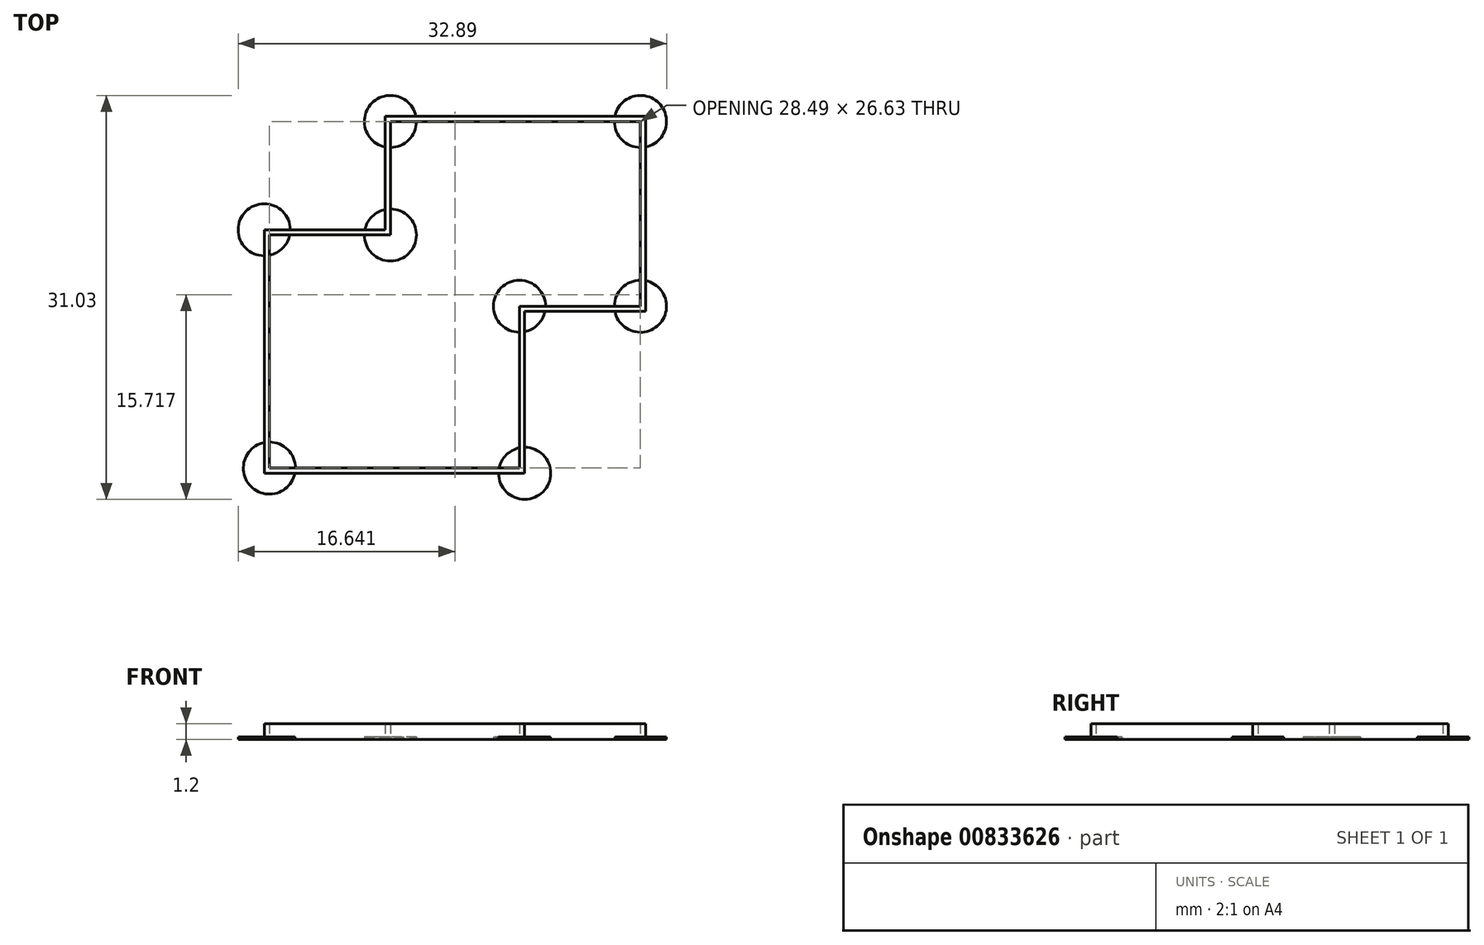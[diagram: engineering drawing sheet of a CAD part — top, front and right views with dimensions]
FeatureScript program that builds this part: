
annotation { "Feature Type Name" : "Feature", "Feature Type Description" : "" }
export const myFeature = defineFeature(function(context is Context, id is Id, definition is map)
    precondition{}
    {
        {
            var Q0;
            Q0=qCreatedBy(makeId("Top.planeOp"),FACE);
            var sketch = newSketch(context, id + "F0", { "sketchPlane" : qUnion([Q0])});
            skLineSegment(sketch, "E0.bottom", {"start": v(-13.81, 9.48) * mm, "end": v(-4.52, 9.48) * mm});
            skLineSegment(sketch, "E0.top", {"start": v(-13.81, -9.23) * mm, "end": v(6.19, -9.23) * mm});
            skLineSegment(sketch, "E0.left", {"start": v(-13.81, 9.48) * mm, "end": v(-13.81, -9.23) * mm});
            skLineSegment(sketch, "E0.right", {"start": v(6.19, 3.2) * mm, "end": v(6.19, -9.23) * mm});
            skLineSegment(sketch, "E1.bottom", {"start": v(-4.52, 18.2) * mm, "end": v(15.48, 18.2) * mm});
            skLineSegment(sketch, "E1.top", {"start": v(6.19, 3.2) * mm, "end": v(15.48, 3.2) * mm});
            skLineSegment(sketch, "E1.left", {"start": v(-4.52, 18.2) * mm, "end": v(-4.52, 9.48) * mm});
            skLineSegment(sketch, "E1.right", {"start": v(15.48, 18.2) * mm, "end": v(15.48, 3.2) * mm});
            skLineSegment(sketch, "E2.0", {"start": v(-4.12, 17.8) * mm, "end": v(-4.12, 9.08) * mm});
            skLineSegment(sketch, "E2.1", {"start": v(-13.41, 9.08) * mm, "end": v(-4.12, 9.08) * mm});
            skLineSegment(sketch, "E2.2", {"start": v(-4.12, 17.8) * mm, "end": v(15.08, 17.8) * mm});
            skLineSegment(sketch, "E2.3", {"start": v(-13.41, 9.08) * mm, "end": v(-13.41, -8.83) * mm});
            skLineSegment(sketch, "E2.4", {"start": v(15.08, 17.8) * mm, "end": v(15.08, 3.6) * mm});
            skLineSegment(sketch, "E2.5", {"start": v(5.79, 3.6) * mm, "end": v(15.08, 3.6) * mm});
            skLineSegment(sketch, "E2.6", {"start": v(5.79, 3.6) * mm, "end": v(5.79, -8.83) * mm});
            skLineSegment(sketch, "E2.7", {"start": v(-13.41, -8.83) * mm, "end": v(5.79, -8.83) * mm});
            skSolve(sketch);
        }
        {
            var Q0;
            Q0=makeQuery(id+"F0.imprint","IMPRINT",FACE,{"disambiguationData":[TD([[makeQuery(id+"F0.imprint","IMPRINT",EDGE,{"derivedFrom":sQuery(id+"F0.wireOp",EDGE,"E0.bottom")}),-1.0]])]});
            extrude(context, id + "F1", {"entities" : qUnion([Q0]), "depth" : 1.2 * mm, "offsetDistance" : 25 * mm});
        }
        {
            var Q0;
            Q0=makeQuery(id+"F1.opExtrude","CAP_FACE",FACE,{"disambiguationData":[OSD([sQuery(id+"F0.wireOp",EDGE,"E0.bottom"),sQuery(id+"F0.wireOp",EDGE,"E0.top"),sQuery(id+"F0.wireOp",EDGE,"E0.left"),sQuery(id+"F0.wireOp",EDGE,"E0.right"),sQuery(id+"F0.wireOp",EDGE,"E1.bottom"),sQuery(id+"F0.wireOp",EDGE,"E1.top"),sQuery(id+"F0.wireOp",EDGE,"E1.left"),sQuery(id+"F0.wireOp",EDGE,"E1.right"),sQuery(id+"F0.wireOp",EDGE,"E2.0"),sQuery(id+"F0.wireOp",EDGE,"E2.1"),sQuery(id+"F0.wireOp",EDGE,"E2.2"),sQuery(id+"F0.wireOp",EDGE,"E2.3"),sQuery(id+"F0.wireOp",EDGE,"E2.4"),sQuery(id+"F0.wireOp",EDGE,"E2.5"),sQuery(id+"F0.wireOp",EDGE,"E2.6"),sQuery(id+"F0.wireOp",EDGE,"E2.7")])],"isStart":true});
            var sketch = newSketch(context, id + "F2", { "sketchPlane" : qUnion([Q0])});
            skCircle(sketch, "E3", {"center": v(-13.41, 8.83) * mm, "radius": 2 * mm});
            skCircle(sketch, "E4", {"center": v(15.08, -3.6) * mm, "radius": 2 * mm});
            skCircle(sketch, "E5", {"center": v(15.08, -17.8) * mm, "radius": 2 * mm});
            skCircle(sketch, "E6", {"center": v(-4.12, -17.8) * mm, "radius": 2 * mm});
            skCircle(sketch, "E7", {"center": v(6.19, 9.23) * mm, "radius": 2 * mm});
            skCircle(sketch, "E8", {"center": v(-13.81, -9.48) * mm, "radius": 2 * mm});
            skCircle(sketch, "E9", {"center": v(-4.12, -9.08) * mm, "radius": 2 * mm});
            skCircle(sketch, "E10", {"center": v(5.79, -3.6) * mm, "radius": 2 * mm});
            skSolve(sketch);
        }
        {
            var Q0;
            {var subQ1=makeQuery(id+"F1.opExtrude","CAP_EDGE",EDGE,{"disambiguationData":[OSD([sQuery(id+"F0.wireOp",EDGE,"E0.top")])],"isStart":true});var subQ3=sQuery(id+"F2.wireOp",EDGE,"E3");var subQ7=makeQuery(id+"F2.imprint","INTERSECT",VERTEX,{"derivedFrom":[subQ1,subQ3]});Q0=makeQuery(id+"F2.imprint","IMPRINT",FACE,{"disambiguationData":[TD([[makeQuery(id+"F2.imprint","IMPRINT",EDGE,{"disambiguationData":[TD([[subQ7,1.0]])],"derivedFrom":subQ3}),1.0]])]});}
            var Q1;
            {var subQ0=sQuery(id+"F2.wireOp",EDGE,"E3");var subQ1=makeQuery(id+"F1.opExtrude","CAP_EDGE",EDGE,{"disambiguationData":[OSD([sQuery(id+"F0.wireOp",EDGE,"E2.7")])],"isStart":true});var subQ2=makeQuery(id+"F2.imprint","INTERSECT",VERTEX,{"derivedFrom":[subQ1,subQ0]});Q1=makeQuery(id+"F2.imprint","IMPRINT",FACE,{"disambiguationData":[TD([[makeQuery(id+"F2.imprint","IMPRINT",EDGE,{"disambiguationData":[TD([[subQ2,1.0]])],"derivedFrom":subQ0}),1.0]])]});}
            var Q2;
            {var subQ0=sQuery(id+"F2.wireOp",EDGE,"E3");var subQ1=makeQuery(id+"F1.opExtrude","CAP_EDGE",EDGE,{"disambiguationData":[OSD([sQuery(id+"F0.wireOp",EDGE,"E0.top")])],"isStart":true});var subQ2=makeQuery(id+"F2.imprint","INTERSECT",VERTEX,{"derivedFrom":[subQ1,subQ0]});Q2=makeQuery(id+"F2.imprint","IMPRINT",FACE,{"disambiguationData":[TD([[makeQuery(id+"F2.imprint","IMPRINT",EDGE,{"disambiguationData":[TD([[subQ2,-1.0]])],"derivedFrom":subQ0}),1.0]])]});}
            var Q3;
            {var subQ0=sQuery(id+"F2.wireOp",EDGE,"E7");var subQ1=makeQuery(id+"F1.opExtrude","CAP_EDGE",EDGE,{"disambiguationData":[OSD([sQuery(id+"F0.wireOp",EDGE,"E2.7")])],"isStart":true});var subQ2=makeQuery(id+"F2.imprint","INTERSECT",VERTEX,{"derivedFrom":[subQ1,subQ0]});Q3=makeQuery(id+"F2.imprint","IMPRINT",FACE,{"disambiguationData":[TD([[makeQuery(id+"F2.imprint","IMPRINT",EDGE,{"disambiguationData":[TD([[subQ2,-1.0]])],"derivedFrom":subQ0}),1.0]])]});}
            var Q4;
            {var subQ0=sQuery(id+"F2.wireOp",EDGE,"E7");var subQ5=makeQuery(id+"F1.opExtrude","CAP_EDGE",EDGE,{"disambiguationData":[OSD([sQuery(id+"F0.wireOp",EDGE,"E0.top")])],"isStart":true});var subQ7=makeQuery(id+"F2.imprint","INTERSECT",VERTEX,{"derivedFrom":[subQ5,subQ0]});Q4=makeQuery(id+"F2.imprint","IMPRINT",FACE,{"disambiguationData":[TD([[makeQuery(id+"F2.imprint","IMPRINT",EDGE,{"disambiguationData":[TD([[subQ7,-1.0]])],"derivedFrom":subQ0}),1.0]])]});}
            var Q5;
            {var subQ0=sQuery(id+"F2.wireOp",EDGE,"E7");var subQ1=makeQuery(id+"F1.opExtrude","CAP_EDGE",EDGE,{"disambiguationData":[OSD([sQuery(id+"F0.wireOp",EDGE,"E0.top")])],"isStart":true});var subQ2=makeQuery(id+"F2.imprint","INTERSECT",VERTEX,{"derivedFrom":[subQ1,subQ0]});Q5=makeQuery(id+"F2.imprint","IMPRINT",FACE,{"disambiguationData":[TD([[makeQuery(id+"F2.imprint","IMPRINT",EDGE,{"disambiguationData":[TD([[subQ2,1.0]])],"derivedFrom":subQ0}),1.0]])]});}
            var Q6;
            {var subQ0=sQuery(id+"F2.wireOp",EDGE,"E8");var subQ1=makeQuery(id+"F1.opExtrude","CAP_EDGE",EDGE,{"disambiguationData":[OSD([sQuery(id+"F0.wireOp",EDGE,"E0.bottom")])],"isStart":true});var subQ2=makeQuery(id+"F2.imprint","INTERSECT",VERTEX,{"derivedFrom":[subQ1,subQ0]});Q6=makeQuery(id+"F2.imprint","IMPRINT",FACE,{"disambiguationData":[TD([[makeQuery(id+"F2.imprint","IMPRINT",EDGE,{"disambiguationData":[TD([[subQ2,1.0]])],"derivedFrom":subQ0}),1.0]])]});}
            var Q7;
            {var subQ1=makeQuery(id+"F1.opExtrude","CAP_EDGE",EDGE,{"disambiguationData":[OSD([sQuery(id+"F0.wireOp",EDGE,"E0.bottom")])],"isStart":true});var subQ3=sQuery(id+"F2.wireOp",EDGE,"E8");var subQ9=makeQuery(id+"F2.imprint","INTERSECT",VERTEX,{"derivedFrom":[subQ1,subQ3]});Q7=makeQuery(id+"F2.imprint","IMPRINT",FACE,{"disambiguationData":[TD([[makeQuery(id+"F2.imprint","IMPRINT",EDGE,{"disambiguationData":[TD([[subQ9,-1.0]])],"derivedFrom":subQ3}),1.0]])]});}
            var Q8;
            {var subQ0=sQuery(id+"F2.wireOp",EDGE,"E8");var subQ1=makeQuery(id+"F1.opExtrude","CAP_EDGE",EDGE,{"disambiguationData":[OSD([sQuery(id+"F0.wireOp",EDGE,"E2.1")])],"isStart":true});var subQ2=makeQuery(id+"F2.imprint","INTERSECT",VERTEX,{"derivedFrom":[subQ1,subQ0]});Q8=makeQuery(id+"F2.imprint","IMPRINT",FACE,{"disambiguationData":[TD([[makeQuery(id+"F2.imprint","IMPRINT",EDGE,{"disambiguationData":[TD([[subQ2,-1.0]])],"derivedFrom":subQ0}),1.0]])]});}
            var Q9;
            {var subQ0=sQuery(id+"F2.wireOp",EDGE,"E9");var subQ1=makeQuery(id+"F1.opExtrude","CAP_EDGE",EDGE,{"disambiguationData":[OSD([sQuery(id+"F0.wireOp",EDGE,"E2.1")])],"isStart":true});var subQ2=makeQuery(id+"F2.imprint","INTERSECT",VERTEX,{"derivedFrom":[subQ1,subQ0]});Q9=makeQuery(id+"F2.imprint","IMPRINT",FACE,{"disambiguationData":[TD([[makeQuery(id+"F2.imprint","IMPRINT",EDGE,{"disambiguationData":[TD([[subQ2,1.0]])],"derivedFrom":subQ0}),1.0]])]});}
            var Q10;
            {var subQ1=makeQuery(id+"F1.opExtrude","CAP_EDGE",EDGE,{"disambiguationData":[OSD([sQuery(id+"F0.wireOp",EDGE,"E0.bottom")])],"isStart":true});var subQ3=sQuery(id+"F2.wireOp",EDGE,"E9");var subQ5=makeQuery(id+"F2.imprint","INTERSECT",VERTEX,{"derivedFrom":[subQ1,subQ3]});Q10=makeQuery(id+"F2.imprint","IMPRINT",FACE,{"disambiguationData":[TD([[makeQuery(id+"F2.imprint","IMPRINT",EDGE,{"disambiguationData":[TD([[subQ5,1.0]])],"derivedFrom":subQ3}),1.0]])]});}
            var Q11;
            {var subQ0=sQuery(id+"F2.wireOp",EDGE,"E9");var subQ1=makeQuery(id+"F1.opExtrude","CAP_EDGE",EDGE,{"disambiguationData":[OSD([sQuery(id+"F0.wireOp",EDGE,"E0.bottom")])],"isStart":true});var subQ2=makeQuery(id+"F2.imprint","INTERSECT",VERTEX,{"derivedFrom":[subQ1,subQ0]});Q11=makeQuery(id+"F2.imprint","IMPRINT",FACE,{"disambiguationData":[TD([[makeQuery(id+"F2.imprint","IMPRINT",EDGE,{"disambiguationData":[TD([[subQ2,-1.0]])],"derivedFrom":subQ0}),1.0]])]});}
            var Q12;
            {var subQ0=sQuery(id+"F2.wireOp",EDGE,"E6");var subQ1=makeQuery(id+"F1.opExtrude","CAP_EDGE",EDGE,{"disambiguationData":[OSD([sQuery(id+"F0.wireOp",EDGE,"E2.0")])],"isStart":true});var subQ2=makeQuery(id+"F2.imprint","INTERSECT",VERTEX,{"derivedFrom":[subQ1,subQ0]});Q12=makeQuery(id+"F2.imprint","IMPRINT",FACE,{"disambiguationData":[TD([[makeQuery(id+"F2.imprint","IMPRINT",EDGE,{"disambiguationData":[TD([[subQ2,1.0]])],"derivedFrom":subQ0}),1.0]])]});}
            var Q13;
            {var subQ0=makeQuery(id+"F1.opExtrude","CAP_EDGE",EDGE,{"disambiguationData":[OSD([sQuery(id+"F0.wireOp",EDGE,"E1.left")])],"isStart":true});var subQ3=sQuery(id+"F2.wireOp",EDGE,"E6");var subQ4=makeQuery(id+"F2.imprint","INTERSECT",VERTEX,{"derivedFrom":[subQ0,subQ3]});Q13=makeQuery(id+"F2.imprint","IMPRINT",FACE,{"disambiguationData":[TD([[makeQuery(id+"F2.imprint","IMPRINT",EDGE,{"disambiguationData":[TD([[subQ4,1.0]])],"derivedFrom":subQ3}),1.0]])]});}
            var Q14;
            {var subQ0=sQuery(id+"F2.wireOp",EDGE,"E6");var subQ1=makeQuery(id+"F1.opExtrude","CAP_EDGE",EDGE,{"disambiguationData":[OSD([sQuery(id+"F0.wireOp",EDGE,"E1.left")])],"isStart":true});var subQ2=makeQuery(id+"F2.imprint","INTERSECT",VERTEX,{"derivedFrom":[subQ1,subQ0]});Q14=makeQuery(id+"F2.imprint","IMPRINT",FACE,{"disambiguationData":[TD([[makeQuery(id+"F2.imprint","IMPRINT",EDGE,{"disambiguationData":[TD([[subQ2,-1.0]])],"derivedFrom":subQ0}),1.0]])]});}
            var Q15;
            {var subQ0=sQuery(id+"F2.wireOp",EDGE,"E5");var subQ1=makeQuery(id+"F1.opExtrude","CAP_EDGE",EDGE,{"disambiguationData":[OSD([sQuery(id+"F0.wireOp",EDGE,"E2.4")])],"isStart":true});var subQ2=makeQuery(id+"F2.imprint","INTERSECT",VERTEX,{"derivedFrom":[subQ1,subQ0]});Q15=makeQuery(id+"F2.imprint","IMPRINT",FACE,{"disambiguationData":[TD([[makeQuery(id+"F2.imprint","IMPRINT",EDGE,{"disambiguationData":[TD([[subQ2,-1.0]])],"derivedFrom":subQ0}),1.0]])]});}
            var Q16;
            {var subQ0=makeQuery(id+"F1.opExtrude","CAP_EDGE",EDGE,{"disambiguationData":[OSD([sQuery(id+"F0.wireOp",EDGE,"E1.right")])],"isStart":true});var subQ3=sQuery(id+"F2.wireOp",EDGE,"E5");var subQ7=makeQuery(id+"F2.imprint","INTERSECT",VERTEX,{"derivedFrom":[subQ0,subQ3]});Q16=makeQuery(id+"F2.imprint","IMPRINT",FACE,{"disambiguationData":[TD([[makeQuery(id+"F2.imprint","IMPRINT",EDGE,{"disambiguationData":[TD([[subQ7,-1.0]])],"derivedFrom":subQ3}),1.0]])]});}
            var Q17;
            {var subQ0=sQuery(id+"F2.wireOp",EDGE,"E5");var subQ1=makeQuery(id+"F1.opExtrude","CAP_EDGE",EDGE,{"disambiguationData":[OSD([sQuery(id+"F0.wireOp",EDGE,"E1.right")])],"isStart":true});var subQ2=makeQuery(id+"F2.imprint","INTERSECT",VERTEX,{"derivedFrom":[subQ1,subQ0]});Q17=makeQuery(id+"F2.imprint","IMPRINT",FACE,{"disambiguationData":[TD([[makeQuery(id+"F2.imprint","IMPRINT",EDGE,{"disambiguationData":[TD([[subQ2,1.0]])],"derivedFrom":subQ0}),1.0]])]});}
            var Q18;
            {var subQ0=sQuery(id+"F2.wireOp",EDGE,"E4");var subQ1=makeQuery(id+"F1.opExtrude","CAP_EDGE",EDGE,{"disambiguationData":[OSD([sQuery(id+"F0.wireOp",EDGE,"E1.top")])],"isStart":true});var subQ2=makeQuery(id+"F2.imprint","INTERSECT",VERTEX,{"derivedFrom":[subQ1,subQ0]});Q18=makeQuery(id+"F2.imprint","IMPRINT",FACE,{"disambiguationData":[TD([[makeQuery(id+"F2.imprint","IMPRINT",EDGE,{"disambiguationData":[TD([[subQ2,1.0]])],"derivedFrom":subQ0}),1.0]])]});}
            var Q19;
            {var subQ1=makeQuery(id+"F1.opExtrude","CAP_EDGE",EDGE,{"disambiguationData":[OSD([sQuery(id+"F0.wireOp",EDGE,"E1.top")])],"isStart":true});var subQ3=sQuery(id+"F2.wireOp",EDGE,"E4");var subQ4=makeQuery(id+"F2.imprint","INTERSECT",VERTEX,{"derivedFrom":[subQ1,subQ3]});Q19=makeQuery(id+"F2.imprint","IMPRINT",FACE,{"disambiguationData":[TD([[makeQuery(id+"F2.imprint","IMPRINT",EDGE,{"disambiguationData":[TD([[subQ4,-1.0]])],"derivedFrom":subQ3}),1.0]])]});}
            var Q20;
            {var subQ0=sQuery(id+"F2.wireOp",EDGE,"E4");var subQ1=makeQuery(id+"F1.opExtrude","CAP_EDGE",EDGE,{"disambiguationData":[OSD([sQuery(id+"F0.wireOp",EDGE,"E2.5")])],"isStart":true});var subQ2=makeQuery(id+"F2.imprint","INTERSECT",VERTEX,{"derivedFrom":[subQ1,subQ0]});Q20=makeQuery(id+"F2.imprint","IMPRINT",FACE,{"disambiguationData":[TD([[makeQuery(id+"F2.imprint","IMPRINT",EDGE,{"disambiguationData":[TD([[subQ2,-1.0]])],"derivedFrom":subQ0}),1.0]])]});}
            var Q21;
            {var subQ0=sQuery(id+"F2.wireOp",EDGE,"E10");var subQ1=makeQuery(id+"F1.opExtrude","CAP_EDGE",EDGE,{"disambiguationData":[OSD([sQuery(id+"F0.wireOp",EDGE,"E2.5")])],"isStart":true});var subQ2=makeQuery(id+"F2.imprint","INTERSECT",VERTEX,{"derivedFrom":[subQ1,subQ0]});Q21=makeQuery(id+"F2.imprint","IMPRINT",FACE,{"disambiguationData":[TD([[makeQuery(id+"F2.imprint","IMPRINT",EDGE,{"disambiguationData":[TD([[subQ2,1.0]])],"derivedFrom":subQ0}),1.0]])]});}
            var Q22;
            {var subQ0=makeQuery(id+"F1.opExtrude","CAP_EDGE",EDGE,{"disambiguationData":[OSD([sQuery(id+"F0.wireOp",EDGE,"E1.top")])],"isStart":true});var subQ3=sQuery(id+"F2.wireOp",EDGE,"E10");var subQ4=makeQuery(id+"F2.imprint","INTERSECT",VERTEX,{"derivedFrom":[subQ0,subQ3]});Q22=makeQuery(id+"F2.imprint","IMPRINT",FACE,{"disambiguationData":[TD([[makeQuery(id+"F2.imprint","IMPRINT",EDGE,{"disambiguationData":[TD([[subQ4,1.0]])],"derivedFrom":subQ3}),1.0]])]});}
            var Q23;
            {var subQ0=sQuery(id+"F2.wireOp",EDGE,"E10");var subQ1=makeQuery(id+"F1.opExtrude","CAP_EDGE",EDGE,{"disambiguationData":[OSD([sQuery(id+"F0.wireOp",EDGE,"E1.top")])],"isStart":true});var subQ2=makeQuery(id+"F2.imprint","INTERSECT",VERTEX,{"derivedFrom":[subQ1,subQ0]});Q23=makeQuery(id+"F2.imprint","IMPRINT",FACE,{"disambiguationData":[TD([[makeQuery(id+"F2.imprint","IMPRINT",EDGE,{"disambiguationData":[TD([[subQ2,-1.0]])],"derivedFrom":subQ0}),1.0]])]});}
            extrude(context, id + "F3", {"entities" : qUnion([Q0, Q1, Q2, Q3, Q4, Q5, Q6, Q7, Q8, Q9, Q10, Q11, Q12, Q13, Q14, Q15, Q16, Q17, Q18, Q19, Q20, Q21, Q22, Q23]), "operationType" : NewBodyOperationType.ADD, "oppositeDirection" : true, "depth" : 0.2 * mm, "offsetDistance" : 25 * mm});
        }
    });
